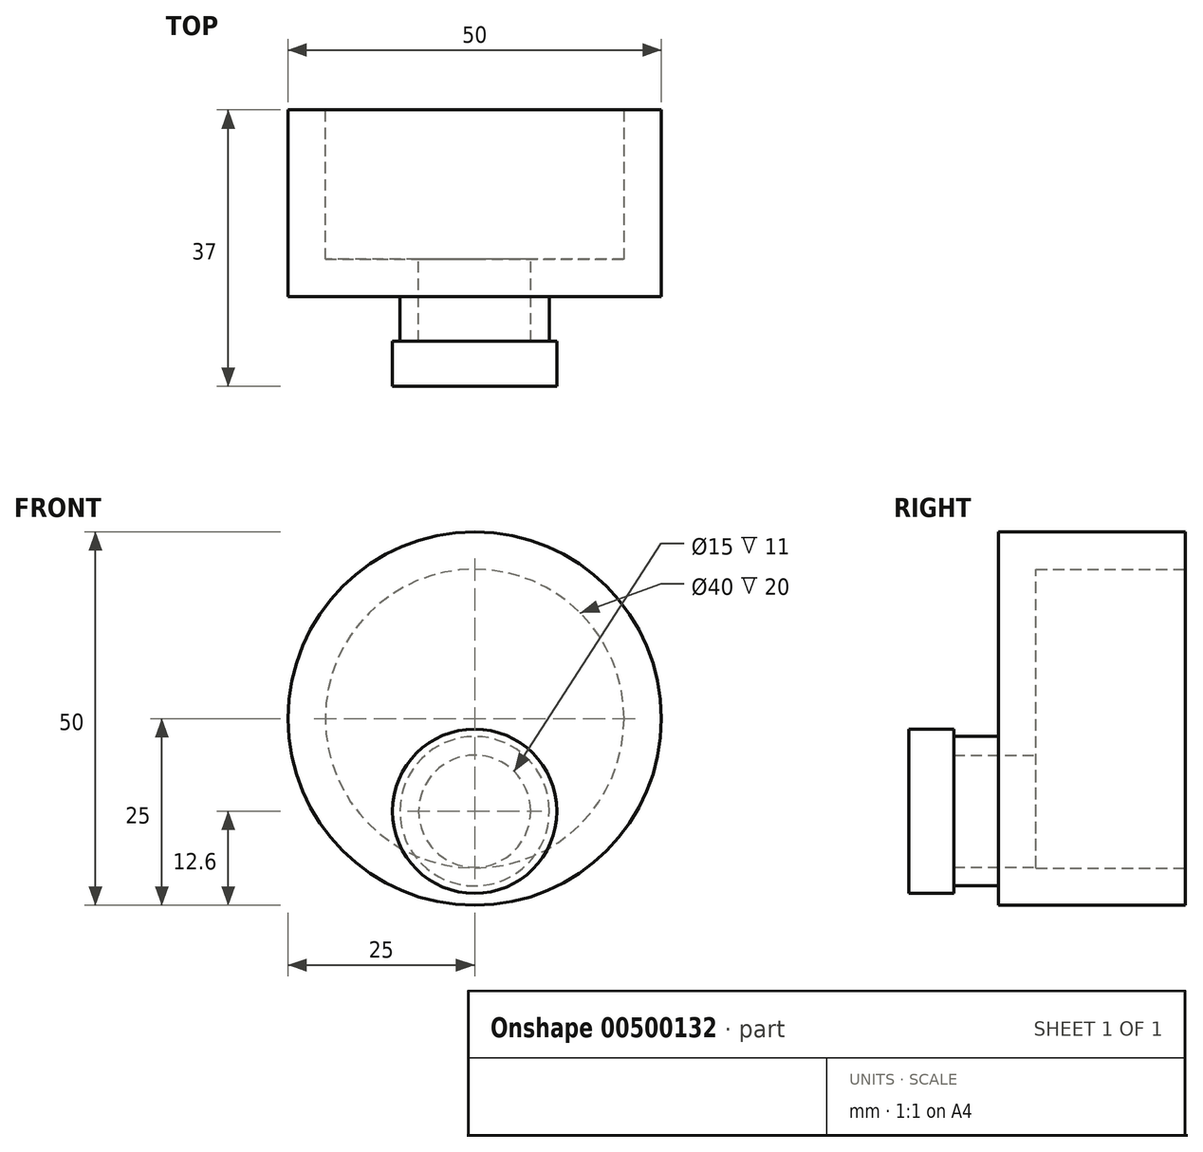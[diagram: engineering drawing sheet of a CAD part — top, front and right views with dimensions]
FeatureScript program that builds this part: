
annotation { "Feature Type Name" : "Feature", "Feature Type Description" : "" }
export const myFeature = defineFeature(function(context is Context, id is Id, definition is map)
    precondition{}
    {
        {
            var Q0;
            Q0=qCreatedBy(makeId("Front.planeOp"),FACE);
            var sketch = newSketch(context, id + "F0", { "sketchPlane" : qUnion([Q0])});
            skCircle(sketch, "E0", {"center": v(0, 0) * mm, "radius": 25 * mm});
            skCircle(sketch, "E1", {"center": v(0, 0) * mm, "radius": 20 * mm});
            skSolve(sketch);
        }
        {
            var Q0;
            Q0=makeQuery(id+"F0.imprint","IMPRINT",FACE,{"disambiguationData":[TD([[makeQuery(id+"F0.imprint","IMPRINT",EDGE,{"derivedFrom":sQuery(id+"F0.wireOp",EDGE,"E0")}),1.0]])]});
            extrude(context, id + "F1", {"entities" : qUnion([Q0]), "depth" : 20 * mm});
        }
        {
            var Q0;
            Q0=makeQuery(id+"F1.opExtrude","CAP_FACE",FACE,{"disambiguationData":[OSD([sQuery(id+"F0.wireOp",EDGE,"E0"),sQuery(id+"F0.wireOp",EDGE,"E1")])],"isStart":false});
            var sketch = newSketch(context, id + "F2", { "sketchPlane" : qUnion([Q0])});
            skCircle(sketch, "E2", {"center": v(0, 0) * mm, "radius": 25 * mm});
            skCircle(sketch, "E3", {"center": v(0, -12.4) * mm, "radius": 7.5 * mm});
            skCircle(sketch, "E4", {"center": v(0, -12.4) * mm, "radius": 10 * mm});
            skSolve(sketch);
        }
        {
            var Q0;
            Q0 = qSketchRegion(id + "F2", true);
            extrude(context, id + "F3", {"entities" : qUnion([Q0]), "operationType" : NewBodyOperationType.ADD, "depth" : 5 * mm});
        }
        {
            var Q0;
            Q0=makeQuery(id+"F2.imprint","IMPRINT",FACE,{"disambiguationData":[TD([[makeQuery(id+"F2.imprint","IMPRINT",EDGE,{"derivedFrom":sQuery(id+"F2.wireOp",EDGE,"E3")}),-1.0]])]});
            var Q1;
            {var subQ0=sQuery(id+"F2.wireOp",EDGE,"E4");var subQ1=makeQuery(id+"F1.opExtrude","CAP_EDGE",EDGE,{"disambiguationData":[OSD([sQuery(id+"F0.wireOp",EDGE,"E1")])],"isStart":false});var subQ2=makeQuery(id+"F2.imprint","INTERSECT",VERTEX,{"disambiguationData":[OD(0.0)],"derivedFrom":[subQ1,subQ0]});Q1=makeQuery(id+"F2.imprint","IMPRINT",FACE,{"disambiguationData":[TD([[makeQuery(id+"F2.imprint","IMPRINT",EDGE,{"disambiguationData":[TD([[subQ2,-1.0]])],"derivedFrom":subQ0}),1.0]])]});}
            extrude(context, id + "F4", {"entities" : qUnion([Q0, Q1]), "operationType" : NewBodyOperationType.ADD, "depth" : 15 * mm});
        }
        {
            var Q0;
            Q0=makeQuery(id+"F4.opExtrude","CAP_FACE",FACE,{"disambiguationData":[OSD([sQuery(id+"F2.wireOp",EDGE,"E3"),sQuery(id+"F2.wireOp",EDGE,"E4")])],"isStart":false});
            var sketch = newSketch(context, id + "F5", { "sketchPlane" : qUnion([Q0])});
            skCircle(sketch, "E5", {"center": v(0, -12.4) * mm, "radius": 11 * mm});
            skSolve(sketch);
        }
        {
            var Q0;
            Q0=makeQuery(id+"F5.imprint","IMPRINT",FACE,{"disambiguationData":[TD([[makeQuery(id+"F5.imprint","IMPRINT",EDGE,{"derivedFrom":sQuery(id+"F5.wireOp",EDGE,"E5")}),1.0]])]});
            var Q1;
            Q1=makeQuery(id+"F5.imprint","IMPRINT",FACE,{"disambiguationData":[TD([[makeQuery(id+"F5.imprint","IMPRINT",EDGE,{"derivedFrom":makeQuery(id+"F4.opExtrude","CAP_EDGE",EDGE,{"disambiguationData":[OSD([sQuery(id+"F2.wireOp",EDGE,"E3")])],"isStart":false})}),-1.0]])]});
            var Q2;
            Q2=makeQuery(id+"F5.imprint","IMPRINT",FACE,{"disambiguationData":[TD([[makeQuery(id+"F5.imprint","IMPRINT",EDGE,{"derivedFrom":makeQuery(id+"F4.opExtrude","CAP_EDGE",EDGE,{"disambiguationData":[OSD([sQuery(id+"F2.wireOp",EDGE,"E3")])],"isStart":false})}),1.0]])]});
            extrude(context, id + "F6", {"entities" : qUnion([Q0, Q1, Q2]), "depth" : 2 * mm});
        }
        {
            var Q0;
            {var subQ0=sQuery(id+"F5.wireOp",EDGE,"E5");Q0=makeQuery(id+"F6.boolean.opBoolean","SPLIT",FACE,{"disambiguationData":[TD([makeQuery(id+"F4.opExtrude","SWEPT_FACE",FACE,{"disambiguationData":[OSD([sQuery(id+"F2.wireOp",EDGE,"E4")])]})])],"derivedFrom":makeQuery(id+"F6.opExtrude","CAP_FACE",FACE,{"disambiguationData":[OSD([subQ0])],"isStart":true})});}
            extrude(context, id + "F7", {"entities" : qUnion([Q0]), "operationType" : NewBodyOperationType.ADD, "depth" : 4 * mm});
        }
    });
